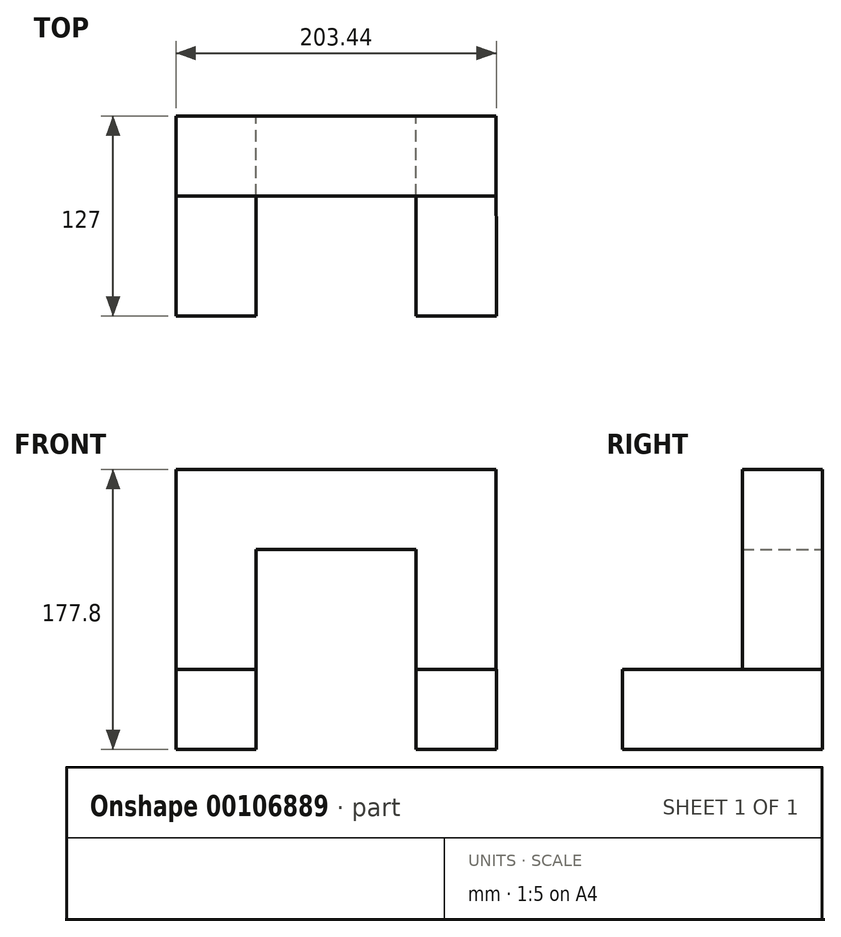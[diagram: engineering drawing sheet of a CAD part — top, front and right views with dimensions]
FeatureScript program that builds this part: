
annotation { "Feature Type Name" : "Feature", "Feature Type Description" : "" }
export const myFeature = defineFeature(function(context is Context, id is Id, definition is map)
    precondition{}
    {
        {
            var Q0;
            Q0=qCreatedBy(makeId("Front.planeOp"),FACE);
            var sketch = newSketch(context, id + "F0", { "sketchPlane" : qUnion([Q0])});
            skLineSegment(sketch, "E0", {"start": v(-98.2, -56.68) * mm, "end": v(-98.2, 70.32) * mm});
            skLineSegment(sketch, "E1", {"start": v(-98.2, 70.32) * mm, "end": v(105, 70.32) * mm});
            skLineSegment(sketch, "E2", {"start": v(105, 70.32) * mm, "end": v(105, -56.68) * mm});
            skLineSegment(sketch, "E3", {"start": v(105, -56.68) * mm, "end": v(54.2, -56.68) * mm});
            skLineSegment(sketch, "E4", {"start": v(54.2, -56.68) * mm, "end": v(54.2, 19.52) * mm});
            skLineSegment(sketch, "E5", {"start": v(54.2, 19.52) * mm, "end": v(-47.4, 19.52) * mm});
            skLineSegment(sketch, "E6", {"start": v(-47.4, 19.52) * mm, "end": v(-47.4, -56.68) * mm});
            skLineSegment(sketch, "E7", {"start": v(-47.4, -56.68) * mm, "end": v(-98.2, -56.68) * mm});
            skSolve(sketch);
        }
        {
            var Q0;
            Q0 = qSketchRegion(id + "F0", true);
            extrude(context, id + "F1", {"entities" : qUnion([Q0]), "depth" : 50.8 * mm});
        }
        {
            var Q0;
            Q0=makeQuery(id+"F1.opExtrude","SWEPT_FACE",FACE,{"disambiguationData":[OSD([sQuery(id+"F0.wireOp",EDGE,"E7")])]});
            var sketch = newSketch(context, id + "F2", { "sketchPlane" : qUnion([Q0])});
            skLineSegment(sketch, "E8", {"start": v(-98.2, 0) * mm, "end": v(-98.2, 127) * mm});
            skLineSegment(sketch, "E9", {"start": v(-98.2, 127) * mm, "end": v(-47.4, 127) * mm});
            skLineSegment(sketch, "E10", {"start": v(-47.4, 127) * mm, "end": v(-47.4, 0) * mm});
            skLineSegment(sketch, "E11", {"start": v(-47.4, 0) * mm, "end": v(-98.2, 0) * mm});
            skSolve(sketch);
        }
        {
            var Q0;
            Q0 = qSketchRegion(id + "F2", true);
            extrude(context, id + "F3", {"entities" : qUnion([Q0]), "operationType" : NewBodyOperationType.ADD, "depth" : 50.8 * mm});
        }
        {
            var Q0;
            Q0=makeQuery(id+"F1.opExtrude","SWEPT_FACE",FACE,{"disambiguationData":[OSD([sQuery(id+"F0.wireOp",EDGE,"E3")])]});
            var sketch = newSketch(context, id + "F4", { "sketchPlane" : qUnion([Q0])});
            skLineSegment(sketch, "E12", {"start": v(54.2, 0) * mm, "end": v(54.2, 127) * mm});
            skLineSegment(sketch, "E13", {"start": v(54.2, 127) * mm, "end": v(105.25, 127) * mm});
            skLineSegment(sketch, "E14", {"start": v(105.25, 127) * mm, "end": v(105, 0) * mm});
            skLineSegment(sketch, "E15", {"start": v(105, 0) * mm, "end": v(54.2, 0) * mm});
            skSolve(sketch);
        }
        {
            var Q0;
            Q0 = qSketchRegion(id + "F4", true);
            extrude(context, id + "F5", {"entities" : qUnion([Q0]), "operationType" : NewBodyOperationType.ADD, "depth" : 50.8 * mm});
        }
    });
